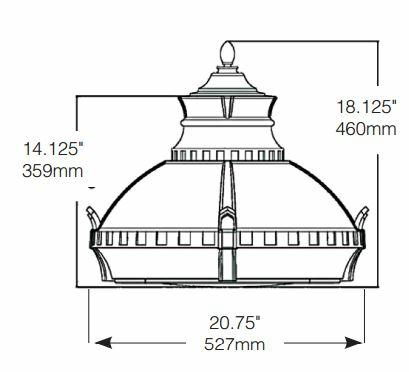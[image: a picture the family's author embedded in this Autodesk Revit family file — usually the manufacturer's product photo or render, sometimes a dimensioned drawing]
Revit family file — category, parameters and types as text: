
# Revit family: PROB
name_source: partatom
category: Lighting Fixtures
revit_build: Autodesk Revit MEP 2012 (Build: 20110309_2315(x64)
units: mm (PartAtom-declared; Revit-internal decimal feet)

## types (13) — shared parameters
Default Elevation = 48.000"
Description = Providence Bollard - PROB
Glass = Hubbell-Glass-Frosted
Lamp = ED-17
Load Classification = Lighting
Manufacturer = Architectural Area Lighting
Manufacturer Fax = (626)-369-2695
Model = PROB
Product Documentation Link = http://cdn.aal.net
Product Page URL = http://www.aal.net
URL = http://www.aal.net
Watt = 25 W
Wattage Comments = 25-43W

## per-type parameters (varying)
| type | Apparent Load | Finish |
| PROB - AWT | 0 VA | Hubbell-Aluminum-Artic White |
| PROB - BLK | 0 VA | Hubbell-Aluminum-Black |
| PROB - MTB | 0 VA | Hubbell-Aluminum-Matte Black |
| PROB - DGN | 0 VA | Hubbell-Aluminum-Dark Green |
| PROB - DBZ | 0 VA | Hubbell-Aluminum-Dark Bronze |
| PROB - WRZ | 0 VA | Hubbell-Aluminum-Weathered Bronze |
| PROB - BRM | 25 VA | Hubbell-Aluminum-Metalic Bronze |
| PROB - VBL | 0 VA | Hubbell-Aluminum-Verde Blue |
| PROB - CRT | 0 VA | Hubbell-Aluminum-Corten |
| PROB - MAL | 0 VA | Hubbell-Aluminum-Matte |
| PROB - MDG | 0 VA | Hubbell-Aluminum-Medium Grey |
| PROB - ATG | 0 VA | Hubbell-Aluminum-Antique Green |
| PROB - LGY | 0 VA | Hubbell-Aluminum-Light Grey |

## geometry (parser evidence)
native form markers: Blend x20, Sweep x6
no freeform markers — native parametric forms only
